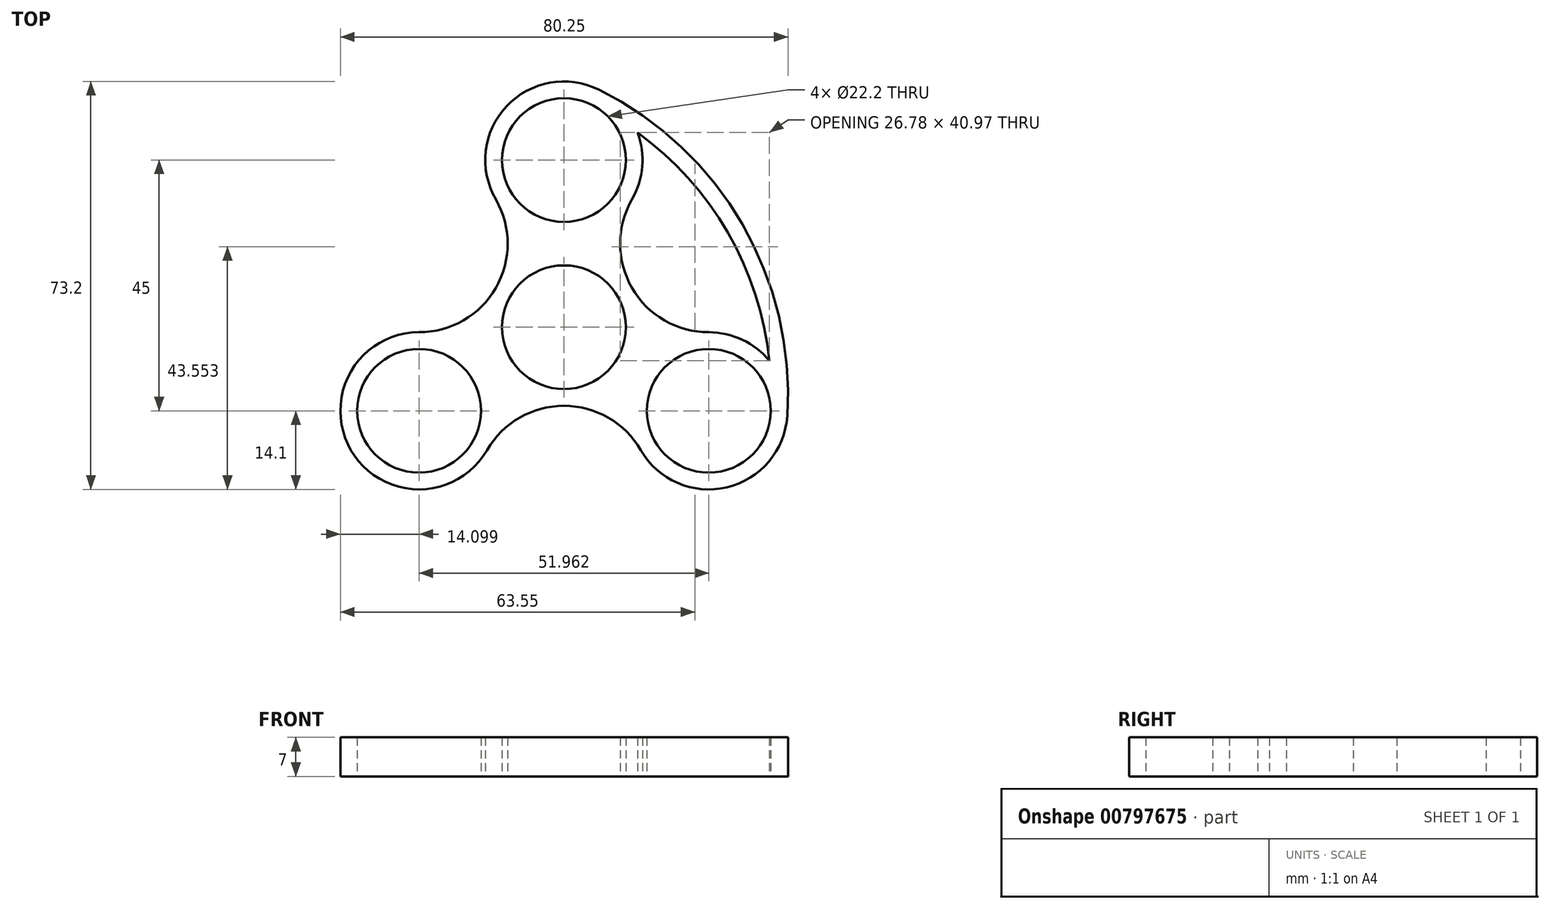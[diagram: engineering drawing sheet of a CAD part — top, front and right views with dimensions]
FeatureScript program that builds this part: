
annotation { "Feature Type Name" : "Feature", "Feature Type Description" : "" }
export const myFeature = defineFeature(function(context is Context, id is Id, definition is map)
    precondition{}
    {
        {
            var Q0;
            Q0=qCreatedBy(makeId("Top.planeOp"),FACE);
            var sketch = newSketch(context, id + "F0", { "sketchPlane" : qUnion([Q0])});
            skCircle(sketch, "E0", {"center": v(0, 0) * mm, "radius": 11.1 * mm});
            skCircle(sketch, "E1.cCircle", {"center": v(0, 0) * mm, "radius": 15 * mm, "construction": true});
            skLineSegment(sketch, "E1.0", {"start": v(25.98, -15) * mm, "end": v(-25.98, -15) * mm, "construction": true});
            skLineSegment(sketch, "E1.1", {"start": v(-25.98, -15) * mm, "end": v(0, 30) * mm, "construction": true});
            skLineSegment(sketch, "E1.2", {"start": v(0, 30) * mm, "end": v(25.98, -15) * mm, "construction": true});
            skPoint(sketch, "E1.0.midPoint", {"position": v(0, -15) * mm});
            skCircle(sketch, "E2", {"center": v(0, 30) * mm, "radius": 11.1 * mm});
            skLineSegment(sketch, "E3", {"start": v(0, 0) * mm, "end": v(-13, 7.5) * mm});
            skLineSegment(sketch, "E4", {"start": v(-13, 7.5) * mm, "end": v(13, 7.5) * mm, "construction": true});
            skLineSegment(sketch, "E5", {"start": v(13, 7.5) * mm, "end": v(0, 0) * mm});
            skLineSegment(sketch, "E6", {"start": v(0, -15) * mm, "end": v(0, 0) * mm, "construction": true});
            skLineSegment(sketch, "E7", {"start": v(13, 7.5) * mm, "end": v(0, -15) * mm, "construction": true});
            skLineSegment(sketch, "E8", {"start": v(-13, 7.5) * mm, "end": v(0, -15) * mm, "construction": true});
            skLineSegment(sketch, "E9", {"start": v(13, 7.5) * mm, "end": v(25.98, 15) * mm, "construction": true});
            skArc(sketch, "E10", {"start": v(12.21, 22.95) * mm, "mid": v(0, 44.1) * mm, "end": v(-12.21, 22.95) * mm});
            skArc(sketch, "E11", {"start": v(12.21, 7.05) * mm, "mid": v(10.08, 15) * mm, "end": v(12.21, 22.95) * mm});
            skArc(sketch, "E12.MirrorCS", {"start": v(-12.21, 7.05) * mm, "mid": v(-10.08, 15) * mm, "end": v(-12.21, 22.95) * mm});
            skCircle(sketch, "E13", {"center": v(0, 0) * mm, "radius": 14.1 * mm, "construction": true});
            skLineSegment(sketch, "E14", {"start": v(-13, 7.5) * mm, "end": v(-12.21, 7.05) * mm});
            skLineSegment(sketch, "E15", {"start": v(12.21, 7.05) * mm, "end": v(13, 7.5) * mm});
            skSolve(sketch);
        }
        {
            var Q0;
            Q0=makeQuery(id+"F0.imprint","IMPRINT",FACE,{"disambiguationData":[TD([[makeQuery(id+"F0.imprint","IMPRINT",EDGE,{"derivedFrom":sQuery(id+"F0.wireOp",EDGE,"E2")}),-1.0]])]});
            extrude(context, id + "F1", {"entities" : qUnion([Q0]), "depth" : 7 * mm, "offsetDistance" : 25 * mm});
        }
        {
            var Q0;
            Q0=makeQuery(id+"F1.opExtrude","SWEPT_BODY",BODY,{"disambiguationData":[OSD([sQuery(id+"F0.wireOp",EDGE,"E0"),sQuery(id+"F0.wireOp",EDGE,"E2"),sQuery(id+"F0.wireOp",EDGE,"E3"),sQuery(id+"F0.wireOp",EDGE,"E5"),sQuery(id+"F0.wireOp",EDGE,"E10"),sQuery(id+"F0.wireOp",EDGE,"FyzykIo4-7ABL-2cN2-SJu5-aql6egmz9Ra5"),sQuery(id+"F0.wireOp",EDGE,"948eeb6a-f036-419e-b3b6-321a4cbb431c0.MirrorCS")])]});
            var Q1;
            Q1=sQuery(id+"F0.wireOp",EDGE,"E0");
            circularPattern(context, id + "F2", {"operationType" : NewBodyOperationType.ADD, "entities" : qUnion([Q0]), "axis" : qUnion([Q1]), "angle" : 360 * degree, "instanceCount" : 3, "equalSpace" : true});
        }
        {
            var Q0;
            Q0=makeQuery(id+"F0.imprint","IMPRINT",FACE,{"disambiguationData":[TD([[makeQuery(id+"F0.imprint","IMPRINT",EDGE,{"derivedFrom":sQuery(id+"F0.wireOp",EDGE,"E2")}),-1.0]])]});
            var sketch = newSketch(context, id + "F3", { "sketchPlane" : qUnion([Q0])});
            skArc(sketch, "E16", {"start": v(40.05, -15.88) * mm, "mid": v(32, 18.47) * mm, "end": v(6.27, 42.63) * mm});
            skArc(sketch, "E17", {"start": v(13.2, 34.94) * mm, "mid": v(29.4, 16.97) * mm, "end": v(36.86, -6.03) * mm});
            skLineSegment(sketch, "E18", {"start": v(40.05, -15.88) * mm, "end": v(36.86, -6.03) * mm});
            skLineSegment(sketch, "E19", {"start": v(13.2, 34.94) * mm, "end": v(6.27, 42.63) * mm});
            skSolve(sketch);
        }
        {
            var Q0;
            {var subQ0=sQuery(id+"F3.wireOp",EDGE,"E16");Q0=makeQuery(id+"F3.imprint","IMPRINT",FACE,{"disambiguationData":[TD([[makeQuery(id+"F3.imprint","IMPRINT",EDGE,{"derivedFrom":subQ0}),1.0]])]});}
            extrude(context, id + "F4", {"entities" : qUnion([Q0]), "operationType" : NewBodyOperationType.ADD, "depth" : 7 * mm, "offsetDistance" : 25 * mm});
        }
    });
